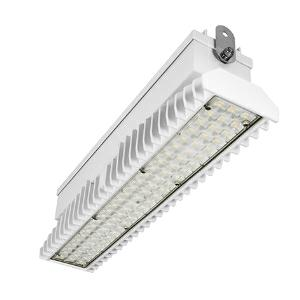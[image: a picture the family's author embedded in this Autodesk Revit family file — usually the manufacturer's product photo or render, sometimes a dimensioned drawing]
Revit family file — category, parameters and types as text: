
# Revit family: 3f_filippi_-_3f_lem_ampio_3f_filippi_-_59157_a0811_-_3f_lem_1_led_50-865_cr_ampio___vt_5375
name_source: partatom
category: Lighting Fixtures
units: mm (PartAtom-declared; Revit-internal decimal feet)

## family parameters
Cut with Voids When Loaded = No
Host = Face
Light Source = No
Part Type = Normal
Room Calculation Point = No
Round Connector Dimension = Use Diameter
Shared = No

## types (1)
- 3F Filippi - 3F LEM Ampio (1 x LED, 7910 lm, 56 W, 6500 K)
    Apparent Load = 56 VA
    Approval mark = CE
    CIE Flux Codes = 60 92 99 100 100
    Color Rendering = 80
    Color Temperature = 6500 K
    Control Gear = Electronic ballast
    Default Elevation = 1800 mm
    Description = Industrial luminaire with high light output and high luminous efficiency designed with the most innovative technologies for environments with temperature up to 55°C.

ILLUMINOTECHNICAL
Luminous efficiency 100% (DLOR 99%, ULOR 1%).
Initial luminous flux of the luminaire 7910 lm.
Direct symmetric wide distribution: the illuminated area has a rectangular shape.
Installation Interdistance Transv.D = 1.58 x hu - Long.D = 1.45 x hu.
Tabular UGR (CIE 117 - 4H-8H; S=0.25H; 70/50/20): RUG 26 - 26.8.
Beam angle: 93° - 99°.
Luminous efficacy 141 lm/W.
Lifetime (L93/B10): 30000 h. (tq+25°C)
Lifetime (L90/B10): 50000 h. (tq+25°C)
Lifetime (L85/B10): 80000 h. (tq+25°C)
Lifetime (L80/B10): 100000 h. (tq+25°C)
Lifetime (L85/B10): 50000 h. (tq+55°C)
Sudden decreased luminous flux after 50000 hours: 0% (C0).
Photobiological safety in compliance with IEC/TR 62778: RG0 risk exempt, (IEC 62471).
In compliance with IEC/EN 62722-2-1 - IEC/EN 62717 standards.

SOURCE
Mid-Power linear LED module 50W/865.
Energy efficiency class (UE 2019/2020 - UE 2019/2015): C.
CIE 13.3 Colour rendering index: CRI >80 (R9 <50%).
IES TM-30 Fidelity Index: Rf = 84 Rg = 95.
CCT nominal colour temperature 6500 K.
Colour initial tolerance (MacAdam): SDCM 3.

MECHANICAL
Passive modular heatsinks in die-casted aluminium, painted in white colour.
To optimize the thermal management of the LED module, the heatsinks are oversized and provided with self-cleaning of cooling fins.
Wiring body in aluminium and galvanised steel anchored solidly to the sinks and thermally separated.
3F Lens lenses with high luminous efficiency, transparent methacrylate (PMMA), fixed to the LED modules.
Fixing brackets in stainless steel.
Luminaire with limited surface temperature. - D - (EN 60598-2-24)
Dimensions: 542x115 mm, height 154 mm. Weight 7.237 kg.
IP65 protection degree.
Mechanical strength to impacts IK06 (1 joule).
Glow-wire test resistance 650°C.

ELECTRICAL
Halogen Free electronic wiring 230V-50/60Hz, power factor 0.95, THD <25%, constant output current, class I, 1 driver.
Power of the luminaire 56 W.
ENEC - CE.
SAFE FLICKER: PstLM=<1 and SVM=<0.4 (IEC TR 61547-1 and IEC TR 63158), to ensure a more comfortable and safe light.
Luminaire compliant with EN 60598-2-22 for power supply from a centralised emergency system CPSS (Central Power Supply System), not incorporated in the luminaire - high risk areas excluded. The default power and flux are 100% in AC and 100% in DC.
Ambient temperature from -30°C to +55°C.
Temperature class T6 max 85°C.
Quick connection via M20 3P connector with 9-13 mm tightening range.
Power unit positioned on a separate compartment by the LED module to ensure optimum temperatures of cabling components, to be inspectable and maintainable.
Relative humidity UR: <85%.

INSTALLATION
Ceiling / Suspended / Wall.
All accessories dedicated to this product are available on the Catalog and on our website www.3F-Filippi.com.

ACCESSORIES
A0811 - VT transparent glass, tempered, not flammable, with sealing gasket.
One required for each light module. The pack contains 10 pieces.

APPLICATIONS
In commercial environments, exhibition and industrial areas, stores, open areas.
Applications with high ambient temperature up to 55°C.
Environments in which it is necessary a total protection against falling fragments (eg environments with foodstuffs or machines with moving parts or with extreme temperature changes), use luminaires with polycarbonate lenses.

WARNING
Fixture not suitable for cold stores with an ambient temperature <0°C and/or relative humidity >85%.
Luminaire designed for disposal/recycling at end-of-life.
Replaceable (LED only) light source by a professional. Replaceable control gear by a professional.
    Height = 154 mm
    Lamp = 1 x LED
    Lamp Light Flux = 7910 lm
    Lamp Power = 56 W
    Lamp count = 1
    Length = 542 mm
    Lifetime = 50000 h
    Luminous efficacy = 141 lm/W
    Manufacturer = 3F Filippi
    ModVariant = No
    Model = 3F Filippi - 59157+A0811 - 3F LEM 1 LED 50-865 CR AMPIO + VT
    Mounting Place = Ceiling
    Mounting Type = Pendant
    Number of Poles = 1
    OnlyDefault = Yes
    Power Factor = 1
    Product Name = 3F Filippi - 3F LEM Ampio
    Product group = pendant luminaire
    ProductGroupID = 9
    Protection Class = Protection class I
    Protection Degree = IP 65
    RLX_Detail_Level = 1
    RLX_Emergency_Light_Flux = 0 lm
    RLX_Emergency_Type = 0
    RLX_Emergency_Type_DB = No
    RlxData = <blob elided: 94557 chars, md5=d756e7fd>
    Socket = socket
    Standby Power = 0 W
    System Light Flux = 7910 lm
    System Power = 56 W
    Type Comments = Product without accessories
    Type Image = 3f_filippi_-_lem_1__a0811.jpg
    URL = http://relux.com
    VarID = ---
    Voltage = 0 V
    Weight = 0.00 kg
    Width = 115 mm

## geometry (parser evidence)
native form markers: Blend x4, Sweep x11
no freeform markers — native parametric forms only
